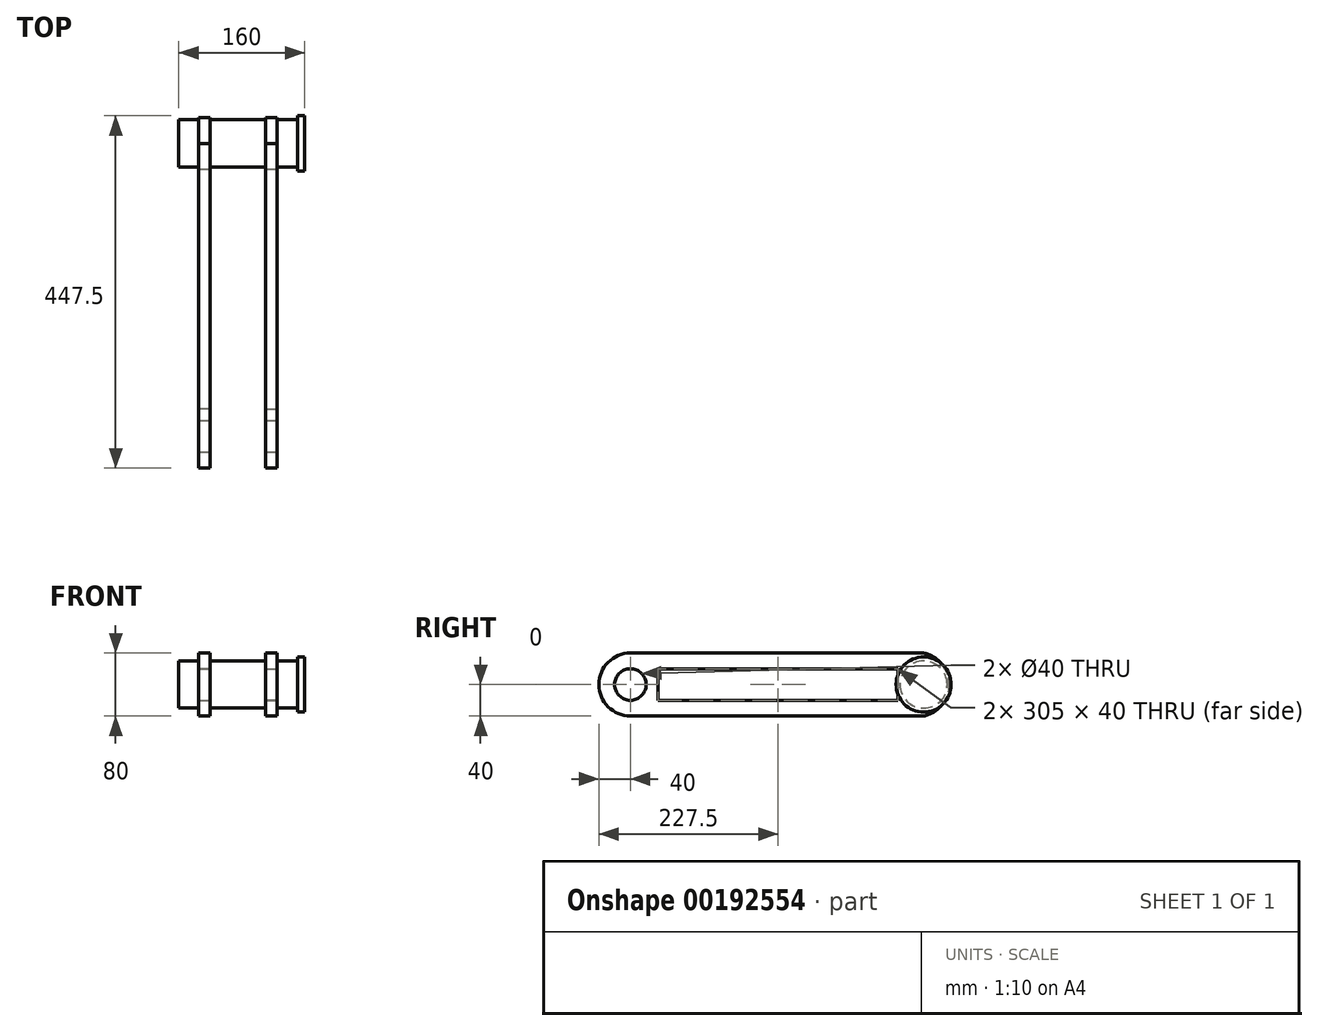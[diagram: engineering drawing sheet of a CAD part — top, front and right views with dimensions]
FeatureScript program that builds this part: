
annotation { "Feature Type Name" : "Feature", "Feature Type Description" : "" }
export const myFeature = defineFeature(function(context is Context, id is Id, definition is map)
    precondition{}
    {
        {
            var Q0;
            Q0=qCreatedBy(makeId("Right.planeOp"),FACE);
            var sketch = newSketch(context, id + "F0", { "sketchPlane" : qUnion([Q0])});
            skCircle(sketch, "E0", {"center": v(0, 0) * mm, "radius": 30 * mm});
            skSolve(sketch);
        }
        {
            var Q0;
            Q0=qSketchRegion(id+"F0",true);
            extrude(context, id + "F1", {"entities" : qUnion([Q0]), "depth" : 160 * mm});
        }
        {
            var Q0;
            Q0=qCreatedBy(makeId("Front.planeOp"),FACE);
            var sketch = newSketch(context, id + "F2", { "sketchPlane" : qUnion([Q0])});
            skLineSegment(sketch, "E1.bottom", {"start": v(25, 40) * mm, "end": v(125, 40) * mm});
            skLineSegment(sketch, "E1.top", {"start": v(25, -40) * mm, "end": v(125, -40) * mm});
            skLineSegment(sketch, "E1.left", {"start": v(25, 40) * mm, "end": v(25, -40) * mm});
            skLineSegment(sketch, "E1.right", {"start": v(125, 40) * mm, "end": v(125, -40) * mm});
            skSolve(sketch);
        }
        {
            var Q0;
            Q0=qSketchRegion(id+"F2",true);
            extrude(context, id + "F3", {"entities" : qUnion([Q0]), "operationType" : NewBodyOperationType.ADD, "depth" : (65 / 2) * mm, "hasSecondDirection" : true, "secondDirectionOppositeDirection" : true, "secondDirectionDepth" : 32.5 * mm});
        }
        {
            var Q0;
            Q0=makeQuery(id+"F3.opExtrude","CAP_FACE",FACE,{"disambiguationData":[OSD([sQuery(id+"F2.wireOp",EDGE,"E1.bottom"),sQuery(id+"F2.wireOp",EDGE,"E1.top"),sQuery(id+"F2.wireOp",EDGE,"E1.left"),sQuery(id+"F2.wireOp",EDGE,"E1.right")])],"isStart":false});
            var sketch = newSketch(context, id + "F4", { "sketchPlane" : qUnion([Q0])});
            skLineSegment(sketch, "E2.bottom", {"start": v(110, 40) * mm, "end": v(125, 40) * mm});
            skLineSegment(sketch, "E2.top", {"start": v(110, 20) * mm, "end": v(125, 20) * mm});
            skLineSegment(sketch, "E2.left", {"start": v(110, 40) * mm, "end": v(110, 20) * mm});
            skLineSegment(sketch, "E2.right", {"start": v(125, 40) * mm, "end": v(125, 20) * mm});
            skLineSegment(sketch, "E3.0.1.0", {"start": v(110, -20) * mm, "end": v(125, -20) * mm});
            skLineSegment(sketch, "E3.0.1.1", {"start": v(110, -40) * mm, "end": v(125, -40) * mm});
            skLineSegment(sketch, "E3.0.1.2", {"start": v(110, -20) * mm, "end": v(110, -40) * mm});
            skLineSegment(sketch, "E3.0.1.3", {"start": v(125, -20) * mm, "end": v(125, -40) * mm});
            skLineSegment(sketch, "E3.1.0.0", {"start": v(25, 40) * mm, "end": v(40, 40) * mm});
            skLineSegment(sketch, "E3.1.0.1", {"start": v(25, 20) * mm, "end": v(40, 20) * mm});
            skLineSegment(sketch, "E3.1.0.2", {"start": v(25, 40) * mm, "end": v(25, 20) * mm});
            skLineSegment(sketch, "E3.1.0.3", {"start": v(40, 40) * mm, "end": v(40, 20) * mm});
            skLineSegment(sketch, "E3.1.1.0", {"start": v(25, -20) * mm, "end": v(40, -20) * mm});
            skLineSegment(sketch, "E3.1.1.1", {"start": v(25, -40) * mm, "end": v(40, -40) * mm});
            skLineSegment(sketch, "E3.1.1.2", {"start": v(25, -20) * mm, "end": v(25, -40) * mm});
            skLineSegment(sketch, "E3.1.1.3", {"start": v(40, -20) * mm, "end": v(40, -40) * mm});
            skLineSegment(sketch, "E3.direction1", {"start": v(110, 20) * mm, "end": v(25, 20) * mm, "construction": true});
            skLineSegment(sketch, "E3.direction2", {"start": v(110, 20) * mm, "end": v(110, -40) * mm, "construction": true});
            skSolve(sketch);
        }
        {
            var Q0;
            Q0=qSketchRegion(id+"F4",true);
            extrude(context, id + "F5", {"entities" : qUnion([Q0]), "operationType" : NewBodyOperationType.ADD, "depth" : 380 * mm});
        }
        {
            var Q0;
            Q0=makeQuery(id+"F5.boolean.opBoolean","MERGE",FACE,{"derivedFrom":[makeQuery(id+"F3.opExtrude","SWEPT_FACE",FACE,{"disambiguationData":[OSD([sQuery(id+"F2.wireOp",EDGE,"E1.right")])]}),makeQuery(id+"F5.opExtrude","SWEPT_FACE",FACE,{"disambiguationData":[OSD([sQuery(id+"F4.wireOp",EDGE,"E2.right")])]}),makeQuery(id+"F5.opExtrude","SWEPT_FACE",FACE,{"disambiguationData":[OSD([sQuery(id+"F4.wireOp",EDGE,"E3.0.1.3")])]})]});
            var sketch = newSketch(context, id + "F6", { "sketchPlane" : qUnion([Q0])});
            skLineSegment(sketch, "E4.bottom", {"start": v(-412.5, 40) * mm, "end": v(-337.5, 40) * mm});
            skLineSegment(sketch, "E4.top", {"start": v(-412.5, -40) * mm, "end": v(-337.5, -40) * mm});
            skLineSegment(sketch, "E4.left", {"start": v(-412.5, 40) * mm, "end": v(-412.5, -40) * mm});
            skLineSegment(sketch, "E4.right", {"start": v(-337.5, 40) * mm, "end": v(-337.5, -40) * mm});
            skSolve(sketch);
        }
        {
            var Q0;
            Q0=qSketchRegion(id+"F6",true);
            extrude(context, id + "F7", {"entities" : qUnion([Q0]), "operationType" : NewBodyOperationType.ADD, "oppositeDirection" : true, "depth" : 15 * mm});
        }
        {
            var Q0;
            Q0=makeQuery(id+"F5.boolean.opBoolean","MERGE",FACE,{"derivedFrom":[makeQuery(id+"F3.opExtrude","SWEPT_FACE",FACE,{"disambiguationData":[OSD([sQuery(id+"F2.wireOp",EDGE,"E1.left")])]}),makeQuery(id+"F5.opExtrude","SWEPT_FACE",FACE,{"disambiguationData":[OSD([sQuery(id+"F4.wireOp",EDGE,"E3.1.0.2")])]}),makeQuery(id+"F5.opExtrude","SWEPT_FACE",FACE,{"disambiguationData":[OSD([sQuery(id+"F4.wireOp",EDGE,"E3.1.1.2")])]})]});
            var sketch = newSketch(context, id + "F8", { "sketchPlane" : qUnion([Q0])});
            skLineSegment(sketch, "E5.bottom", {"start": v(337.5, 40) * mm, "end": v(412.5, 40) * mm});
            skLineSegment(sketch, "E5.top", {"start": v(337.5, -40) * mm, "end": v(412.5, -40) * mm});
            skLineSegment(sketch, "E5.left", {"start": v(337.5, 40) * mm, "end": v(337.5, -40) * mm});
            skLineSegment(sketch, "E5.right", {"start": v(412.5, 40) * mm, "end": v(412.5, -40) * mm});
            skSolve(sketch);
        }
        {
            var Q0;
            Q0=qSketchRegion(id+"F8",true);
            extrude(context, id + "F9", {"entities" : qUnion([Q0]), "operationType" : NewBodyOperationType.ADD, "oppositeDirection" : true, "depth" : 15 * mm});
        }
        {
            var Q0;
            Q0=makeQuery(id+"F9.boolean.opBoolean","MERGE",FACE,{"derivedFrom":[makeQuery(id+"F5.boolean.opBoolean","MERGE",FACE,{"derivedFrom":[makeQuery(id+"F3.opExtrude","SWEPT_FACE",FACE,{"disambiguationData":[OSD([sQuery(id+"F2.wireOp",EDGE,"E1.left")])]}),makeQuery(id+"F5.opExtrude","SWEPT_FACE",FACE,{"disambiguationData":[OSD([sQuery(id+"F4.wireOp",EDGE,"E3.1.0.2")])]}),makeQuery(id+"F5.opExtrude","SWEPT_FACE",FACE,{"disambiguationData":[OSD([sQuery(id+"F4.wireOp",EDGE,"E3.1.1.2")])]})]}),makeQuery(id+"F9.opExtrude","CAP_FACE",FACE,{"disambiguationData":[OSD([sQuery(id+"F8.wireOp",EDGE,"E5.bottom"),sQuery(id+"F8.wireOp",EDGE,"E5.top"),sQuery(id+"F8.wireOp",EDGE,"E5.left"),sQuery(id+"F8.wireOp",EDGE,"E5.right")])],"isStart":true})]});
            var sketch = newSketch(context, id + "F10", { "sketchPlane" : qUnion([Q0])});
            skCircle(sketch, "E6", {"center": v(372.5, 0) * mm, "radius": 20 * mm});
            skSolve(sketch);
        }
        {
            var Q0;
            Q0=qSketchRegion(id+"F10",true);
            extrude(context, id + "F11", {"entities" : qUnion([Q0]), "operationType" : NewBodyOperationType.REMOVE, "endBound" : BoundingType.THROUGH_ALL, "oppositeDirection" : true, "depth" : 25 * mm});
        }
        {
            var Q0;
            Q0=makeQuery(id+"F7.boolean.opBoolean","MERGE",FACE,{"derivedFrom":[makeQuery(id+"F5.boolean.opBoolean","MERGE",FACE,{"derivedFrom":[makeQuery(id+"F3.opExtrude","SWEPT_FACE",FACE,{"disambiguationData":[OSD([sQuery(id+"F2.wireOp",EDGE,"E1.right")])]}),makeQuery(id+"F5.opExtrude","SWEPT_FACE",FACE,{"disambiguationData":[OSD([sQuery(id+"F4.wireOp",EDGE,"E2.right")])]}),makeQuery(id+"F5.opExtrude","SWEPT_FACE",FACE,{"disambiguationData":[OSD([sQuery(id+"F4.wireOp",EDGE,"E3.0.1.3")])]})]}),makeQuery(id+"F7.opExtrude","CAP_FACE",FACE,{"disambiguationData":[OSD([sQuery(id+"F6.wireOp",EDGE,"E4.bottom"),sQuery(id+"F6.wireOp",EDGE,"E4.top"),sQuery(id+"F6.wireOp",EDGE,"E4.left"),sQuery(id+"F6.wireOp",EDGE,"E4.right")])],"isStart":true})]});
            var sketch = newSketch(context, id + "F12", { "sketchPlane" : qUnion([Q0])});
            skArc(sketch, "E7", {"start": v(-372.5, 40) * mm, "mid": v(-412.5, 0) * mm, "end": v(-372.5, -40) * mm});
            skLineSegment(sketch, "E8", {"start": v(-372.5, 40) * mm, "end": v(-412.5, 40) * mm});
            skLineSegment(sketch, "E9", {"start": v(-412.5, 40) * mm, "end": v(-412.5, -40) * mm});
            skLineSegment(sketch, "E10", {"start": v(-412.5, -40) * mm, "end": v(-372.5, -40) * mm});
            skSolve(sketch);
        }
        {
            var Q0;
            Q0 = qSketchRegion(id + "F12", true);
            extrude(context, id + "F13", {"entities" : qUnion([Q0]), "operationType" : NewBodyOperationType.REMOVE, "endBound" : BoundingType.THROUGH_ALL, "oppositeDirection" : true, "depth" : 25 * mm});
        }
        {
            var Q0;
            Q0=makeQuery(id+"F3.opExtrude","CAP_FACE",FACE,{"disambiguationData":[OSD([sQuery(id+"F2.wireOp",EDGE,"E1.bottom"),sQuery(id+"F2.wireOp",EDGE,"E1.top"),sQuery(id+"F2.wireOp",EDGE,"E1.left"),sQuery(id+"F2.wireOp",EDGE,"E1.right")])],"isStart":false});
            var sketch = newSketch(context, id + "F14", { "sketchPlane" : qUnion([Q0])});
            skLineSegment(sketch, "E11.bottom", {"start": v(40, 40) * mm, "end": v(110, 40) * mm});
            skLineSegment(sketch, "E11.top", {"start": v(40, -40) * mm, "end": v(110, -40) * mm});
            skLineSegment(sketch, "E11.left", {"start": v(40, 40) * mm, "end": v(40, -40) * mm});
            skLineSegment(sketch, "E11.right", {"start": v(110, 40) * mm, "end": v(110, -40) * mm});
            skSolve(sketch);
        }
        {
            var Q0;
            Q0 = qSketchRegion(id + "F14", true);
            extrude(context, id + "F15", {"entities" : qUnion([Q0]), "operationType" : NewBodyOperationType.REMOVE, "endBound" : BoundingType.THROUGH_ALL, "oppositeDirection" : true, "depth" : 55 * mm});
        }
        {
            var Q0;
            Q0=makeQuery(id+"F7.boolean.opBoolean","MERGE",FACE,{"derivedFrom":[makeQuery(id+"F5.boolean.opBoolean","MERGE",FACE,{"derivedFrom":[makeQuery(id+"F3.opExtrude","SWEPT_FACE",FACE,{"disambiguationData":[OSD([sQuery(id+"F2.wireOp",EDGE,"E1.right")])]}),makeQuery(id+"F5.opExtrude","SWEPT_FACE",FACE,{"disambiguationData":[OSD([sQuery(id+"F4.wireOp",EDGE,"E2.right")])]}),makeQuery(id+"F5.opExtrude","SWEPT_FACE",FACE,{"disambiguationData":[OSD([sQuery(id+"F4.wireOp",EDGE,"E3.0.1.3")])]})]}),makeQuery(id+"F7.opExtrude","CAP_FACE",FACE,{"disambiguationData":[OSD([sQuery(id+"F6.wireOp",EDGE,"E4.bottom"),sQuery(id+"F6.wireOp",EDGE,"E4.top"),sQuery(id+"F6.wireOp",EDGE,"E4.left"),sQuery(id+"F6.wireOp",EDGE,"E4.right")])],"isStart":true})]});
            var sketch = newSketch(context, id + "F16", { "sketchPlane" : qUnion([Q0])});
            skArc(sketch, "E12", {"start": v(0, -40) * mm, "mid": v(32.5, 0) * mm, "end": v(0, 40) * mm});
            skLineSegment(sketch, "E13", {"start": v(0, 40) * mm, "end": v(32.5, 40) * mm});
            skLineSegment(sketch, "E14", {"start": v(32.5, 40) * mm, "end": v(32.5, -40) * mm});
            skLineSegment(sketch, "E15", {"start": v(32.5, -40) * mm, "end": v(0, -40) * mm});
            skSolve(sketch);
        }
        {
            var Q0;
            Q0 = qSketchRegion(id + "F16", true);
            extrude(context, id + "F17", {"entities" : qUnion([Q0]), "operationType" : NewBodyOperationType.REMOVE, "endBound" : BoundingType.THROUGH_ALL, "oppositeDirection" : true, "depth" : 25 * mm});
        }
        {
            var Q0;
            Q0=makeQuery(id+"F15.boolean.opBoolean","MERGE",FACE,{"derivedFrom":[makeQuery(id+"F7.boolean.opBoolean","MERGE",FACE,{"derivedFrom":[makeQuery(id+"F5.opExtrude","SWEPT_FACE",FACE,{"disambiguationData":[OSD([sQuery(id+"F4.wireOp",EDGE,"E2.left")])]}),makeQuery(id+"F5.opExtrude","SWEPT_FACE",FACE,{"disambiguationData":[OSD([sQuery(id+"F4.wireOp",EDGE,"E3.0.1.2")])]}),makeQuery(id+"F7.opExtrude","CAP_FACE",FACE,{"disambiguationData":[OSD([sQuery(id+"F6.wireOp",EDGE,"E4.bottom"),sQuery(id+"F6.wireOp",EDGE,"E4.top"),sQuery(id+"F6.wireOp",EDGE,"E4.left"),sQuery(id+"F6.wireOp",EDGE,"E4.right")])],"isStart":false})]}),makeQuery(id+"F15.opExtrude","SWEPT_FACE",FACE,{"disambiguationData":[OSD([sQuery(id+"F14.wireOp",EDGE,"E11.right")])]})]});
            var sketch = newSketch(context, id + "F18", { "sketchPlane" : qUnion([Q0])});
            skCircle(sketch, "E16", {"center": v(0, 0) * mm, "radius": 30 * mm});
            skSolve(sketch);
        }
        {
            var Q0;
            Q0 = qSketchRegion(id + "F18", true);
            extrude(context, id + "F19", {"entities" : qUnion([Q0]), "depth" : 70 * mm});
        }
        {
            var Q0;
            Q0=makeQuery(id+"F1.opExtrude","CAP_FACE",FACE,{"disambiguationData":[OSD([sQuery(id+"F0.wireOp",EDGE,"E0")])],"isStart":false});
            var sketch = newSketch(context, id + "F20", { "sketchPlane" : qUnion([Q0])});
            skCircle(sketch, "E17", {"center": v(0, 0) * mm, "radius": 35 * mm});
            skSolve(sketch);
        }
        {
            var Q0;
            Q0 = qSketchRegion(id + "F20", true);
            extrude(context, id + "F21", {"entities" : qUnion([Q0]), "operationType" : NewBodyOperationType.ADD, "oppositeDirection" : true, "depth" : 9 * mm});
        }
    });
